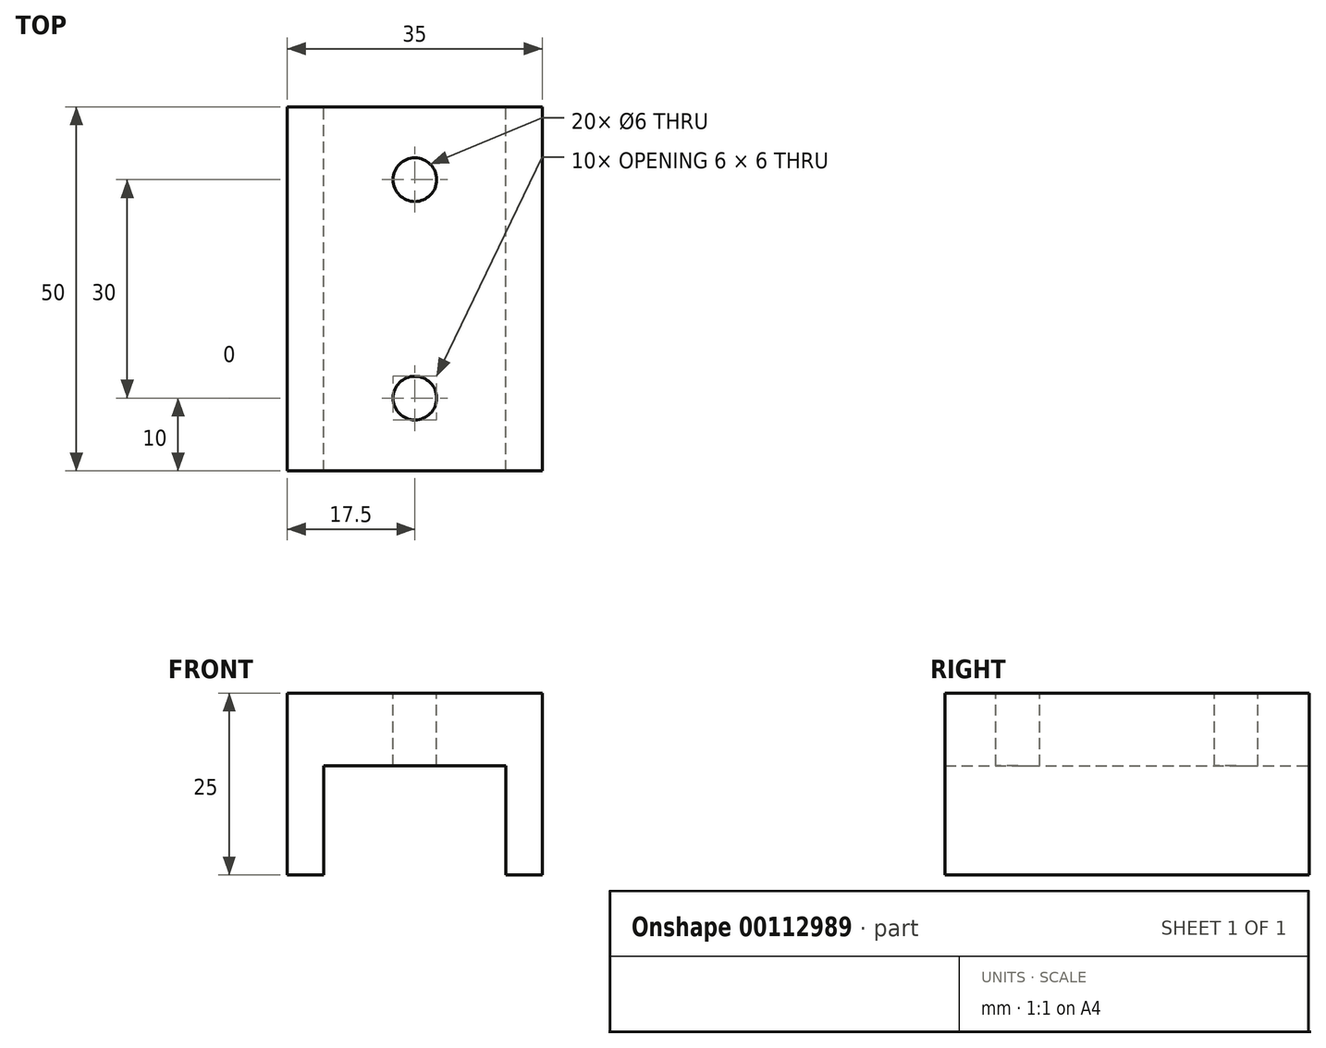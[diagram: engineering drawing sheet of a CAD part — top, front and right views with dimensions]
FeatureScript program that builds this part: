
annotation { "Feature Type Name" : "Feature", "Feature Type Description" : "" }
export const myFeature = defineFeature(function(context is Context, id is Id, definition is map)
    precondition{}
    {
        {
            var Q0;
            Q0=qCreatedBy(makeId("Front.planeOp"),FACE);
            var sketch = newSketch(context, id + "F0", { "sketchPlane" : qUnion([Q0])});
            skLineSegment(sketch, "E0.bottom", {"start": v(-17.5, -12.5) * mm, "end": v(-12.5, -12.5) * mm});
            skLineSegment(sketch, "E0.top", {"start": v(-17.5, 12.5) * mm, "end": v(17.5, 12.5) * mm});
            skLineSegment(sketch, "E0.left", {"start": v(-17.5, -12.5) * mm, "end": v(-17.5, 12.5) * mm});
            skLineSegment(sketch, "E0.right", {"start": v(17.5, -12.5) * mm, "end": v(17.5, 12.5) * mm});
            skPoint(sketch, "E0.middle", {"position": v(0, 0) * mm});
            skLineSegment(sketch, "E1.trimOffspring", {"start": v(12.5, -12.5) * mm, "end": v(17.5, -12.5) * mm});
            skLineSegment(sketch, "E2", {"start": v(12.5, 2.5) * mm, "end": v(-12.5, 2.5) * mm});
            skLineSegment(sketch, "E3", {"start": v(-12.5, 2.5) * mm, "end": v(-12.5, -12.5) * mm});
            skLineSegment(sketch, "E4", {"start": v(12.5, 2.5) * mm, "end": v(12.5, -12.5) * mm});
            skSolve(sketch);
        }
        {
            var Q0;
            Q0=makeQuery(id+"F0.imprint","IMPRINT",FACE,{"disambiguationData":[TD([[makeQuery(id+"F0.imprint","IMPRINT",EDGE,{"derivedFrom":sQuery(id+"F0.wireOp",EDGE,"E0.bottom")}),1.0]])]});
            extrude(context, id + "F1", {"entities" : qUnion([Q0]), "depth" : 50 * mm});
        }
        {
            var Q0;
            Q0=makeQuery(id+"F1.opExtrude","SWEPT_FACE",FACE,{"disambiguationData":[OSD([sQuery(id+"F0.wireOp",EDGE,"E0.top")])]});
            var sketch = newSketch(context, id + "F2", { "sketchPlane" : qUnion([Q0])});
            skCircle(sketch, "E5", {"center": v(0, -10) * mm, "radius": 3 * mm});
            skCircle(sketch, "E6", {"center": v(0, -40) * mm, "radius": 3 * mm});
            skSolve(sketch);
        }
        {
            var Q0;
            Q0=makeQuery(id+"F2.imprint","IMPRINT",FACE,{"disambiguationData":[TD([[makeQuery(id+"F2.imprint","IMPRINT",EDGE,{"derivedFrom":sQuery(id+"F2.wireOp",EDGE,"E5")}),1.0]])]});
            var Q1;
            Q1=makeQuery(id+"F2.imprint","IMPRINT",FACE,{"disambiguationData":[TD([[makeQuery(id+"F2.imprint","IMPRINT",EDGE,{"derivedFrom":sQuery(id+"F2.wireOp",EDGE,"E6")}),1.0]])]});
            extrude(context, id + "F3", {"entities" : qUnion([Q0, Q1]), "operationType" : NewBodyOperationType.REMOVE, "oppositeDirection" : true, "depth" : 25 * mm});
        }
    });
